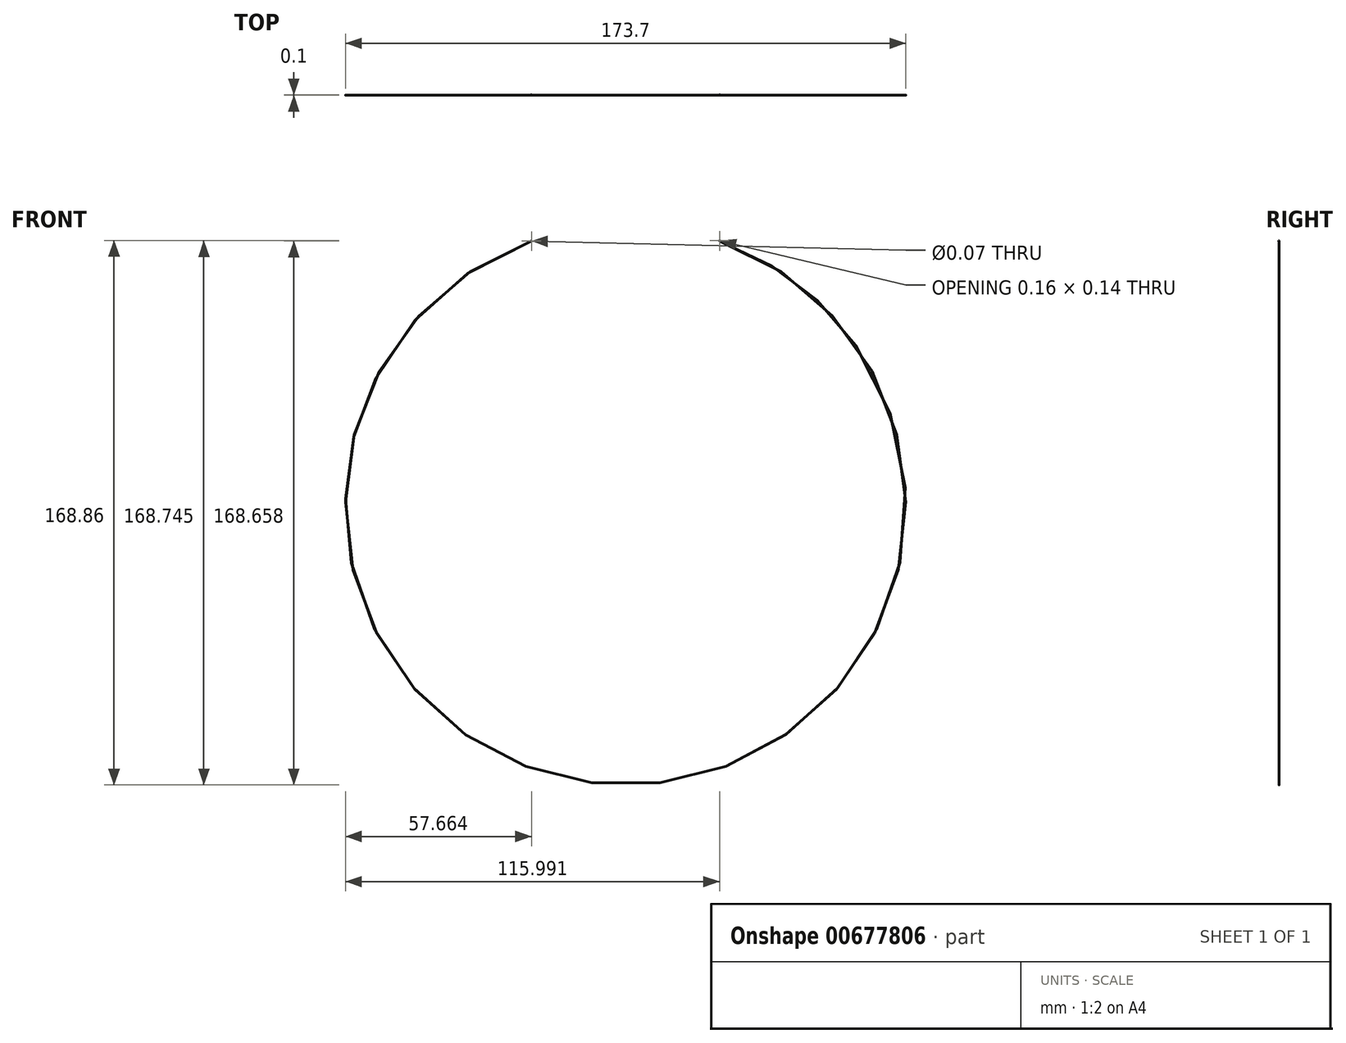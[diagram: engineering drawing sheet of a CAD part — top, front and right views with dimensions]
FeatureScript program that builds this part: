
annotation { "Feature Type Name" : "Feature", "Feature Type Description" : "" }
export const myFeature = defineFeature(function(context is Context, id is Id, definition is map)
    precondition{}
    {
        {
            var Q0;
            Q0=qCreatedBy(makeId("Front.planeOp"),FACE);
            var sketch = newSketch(context, id + "F0", { "sketchPlane" : qUnion([Q0])});
            skArc(sketch, "E0", {"start": v(-27.87, 0) * mm, "mid": v(1.38, -168.6) * mm, "end": v(30.63, 0) * mm});
            skPoint(sketch, "E1.orphan", {"position": v(0, 0) * mm});
            skSolve(sketch);
        }
        {
            var Q0;
            Q0=qCreatedBy(makeId("Top.planeOp"),FACE);
            var sketch = newSketch(context, id + "F1", { "sketchPlane" : qUnion([Q0])});
            skCircle(sketch, "E2", {"center": v(30.64, 0) * mm, "radius": 0.03 * mm});
            skSolve(sketch);
        }
        {
            var Q0;
            Q0=makeQuery(id+"F1.imprint","IMPRINT",FACE,{"disambiguationData":[TD([[makeQuery(id+"F1.imprint","IMPRINT",EDGE,{"derivedFrom":sQuery(id+"F1.wireOp",EDGE,"E2")}),1.0]])]});
            var Q1;
            Q1=sQuery(id+"F0.wireOp",EDGE,"E0");
            sweep(context, id + "F2", {"profiles" : qUnion([Q0]), "path" : qUnion([Q1])});
        }
        {
            var Q0;
            Q0=qCreatedBy(makeId("Front.planeOp"),FACE);
            var sketch = newSketch(context, id + "F3", { "sketchPlane" : qUnion([Q0])});
            skLineSegment(sketch, "E3", {"start": v(-27.97, 0.04) * mm, "end": v(-27.82, 0.1) * mm});
            skLineSegment(sketch, "E4", {"start": v(-27.8, -0.02) * mm, "end": v(-27.93, -0.1) * mm});
            skArc(sketch, "E5", {"start": v(-27.8, -0.02) * mm, "mid": v(-27.76, 0.05) * mm, "end": v(-27.82, 0.1) * mm});
            skCircle(sketch, "E6", {"center": v(-27.8, 0.04) * mm, "radius": 0.04 * mm});
            skArc(sketch, "E7", {"start": v(-27.97, 0.04) * mm, "mid": v(-28.02, 0) * mm, "end": v(-28.03, -0.07) * mm});
            skArc(sketch, "E8", {"start": v(-28.03, -0.07) * mm, "mid": v(-27.98, -0.1) * mm, "end": v(-27.93, -0.1) * mm});
            skSolve(sketch);
        }
        {
            var Q0;
            Q0=makeQuery(id+"F3.imprint","IMPRINT",FACE,{"disambiguationData":[TD([[makeQuery(id+"F3.imprint","IMPRINT",EDGE,{"derivedFrom":sQuery(id+"F3.wireOp",EDGE,"E3")}),-1.0]])]});
            extrude(context, id + "F4", {"entities" : qUnion([Q0]), "operationType" : NewBodyOperationType.ADD, "endBound" : BoundingType.SYMMETRIC, "depth" : 0.1 * mm, "offsetDistance" : 25.4 * mm});
        }
        {
            var Q0;
            Q0=qCreatedBy(makeId("Front.planeOp"),FACE);
            var sketch = newSketch(context, id + "F5", { "sketchPlane" : qUnion([Q0])});
            skArc(sketch, "E9", {"start": v(30.58, -0.03) * mm, "mid": v(30.65, -0.05) * mm, "end": v(30.7, -0.02) * mm});
            skArc(sketch, "E10", {"start": v(30.7, -0.02) * mm, "mid": v(30.7, 0.03) * mm, "end": v(30.67, 0.07) * mm});
            skArc(sketch, "E11", {"start": v(30.67, 0.07) * mm, "mid": v(30.63, 0.2) * mm, "end": v(30.5, 0.24) * mm});
            skArc(sketch, "E12", {"start": v(30.5, 0.24) * mm, "mid": v(30.42, 0.17) * mm, "end": v(30.45, 0.05) * mm});
            skArc(sketch, "E13", {"start": v(30.45, 0.05) * mm, "mid": v(30.46, 0.04) * mm, "end": v(30.47, 0.05) * mm});
            skArc(sketch, "E14", {"start": v(30.53, 0.2) * mm, "mid": v(30.46, 0.15) * mm, "end": v(30.45, 0.07) * mm});
            skArc(sketch, "E15", {"start": v(30.6, 0.07) * mm, "mid": v(30.59, 0.15) * mm, "end": v(30.53, 0.2) * mm});
            skArc(sketch, "E16", {"start": v(30.58, 0.05) * mm, "mid": v(30.57, 0) * mm, "end": v(30.58, -0.03) * mm});
            skPoint(sketch, "E17.orphan", {"position": v(30.53, 0.15) * mm});
            skPoint(sketch, "E18.center.orphan", {"position": v(30.49, 0.1) * mm});
            skArc(sketch, "E19", {"start": v(30.47, 0.05) * mm, "mid": v(30.53, 0.03) * mm, "end": v(30.58, 0.05) * mm});
            skArc(sketch, "E20", {"start": v(30.45, 0.07) * mm, "mid": v(30.52, 0.06) * mm, "end": v(30.6, 0.07) * mm});
            skSolve(sketch);
        }
        {
            var Q0;
            Q0=makeQuery(id+"F5.imprint","IMPRINT",FACE,{"disambiguationData":[TD([[makeQuery(id+"F5.imprint","IMPRINT",EDGE,{"derivedFrom":sQuery(id+"F5.wireOp",EDGE,"E9")}),1.0]])]});
            extrude(context, id + "F6", {"entities" : qUnion([Q0]), "operationType" : NewBodyOperationType.ADD, "endBound" : BoundingType.SYMMETRIC, "depth" : 0.1 * mm, "offsetDistance" : 25.4 * mm});
        }
    });
